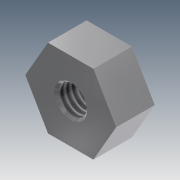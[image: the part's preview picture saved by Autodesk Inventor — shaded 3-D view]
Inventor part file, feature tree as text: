
AUTODESK INVENTOR PART (.ipt)
format: ipt  version: 2013 (Build 170138000, 138)  size: 99,328 bytes
history: native  units: mm
features: chamfer x2, sketch x2, extrude x1, hole x1
ambient origin geometry x8: Origin, YZ Plane, XZ Plane, XY Plane, X Axis, Y Axis, Z Axis, Center Point
bodies: Solid1 (feature_tree)
feature tree (6):
  extrude  "Extrusion1"  Depth=3.4mm TaperAngle=0.0deg
  hole  "Hole1"  [1 undecoded]
  chamfer  "Chamfer1"  Distance=0.2mm Angle=45.0deg
  chamfer  "Chamfer2"  [1 undecoded]
  sketch  "Sketch1"  dims[d0=8.0mm d7=3.4mm d8=0.0mm]
  sketch  "Sketch2"  dims[d9=2.459mm d10=3.4mm d11=4.0mm d12=2.0mm d13=90.0deg d14=3.4mm d15=20.594885mm d16=0.2mm d17=2.0mm d18=45.0deg d19=0.2mm d20=2.0mm d21=45.0deg]
note: 2 required parameter values undecoded (feature->parameter linkage not recoverable at this tier; creation-order binding heuristic only, values carry confidence <= 0.55)
